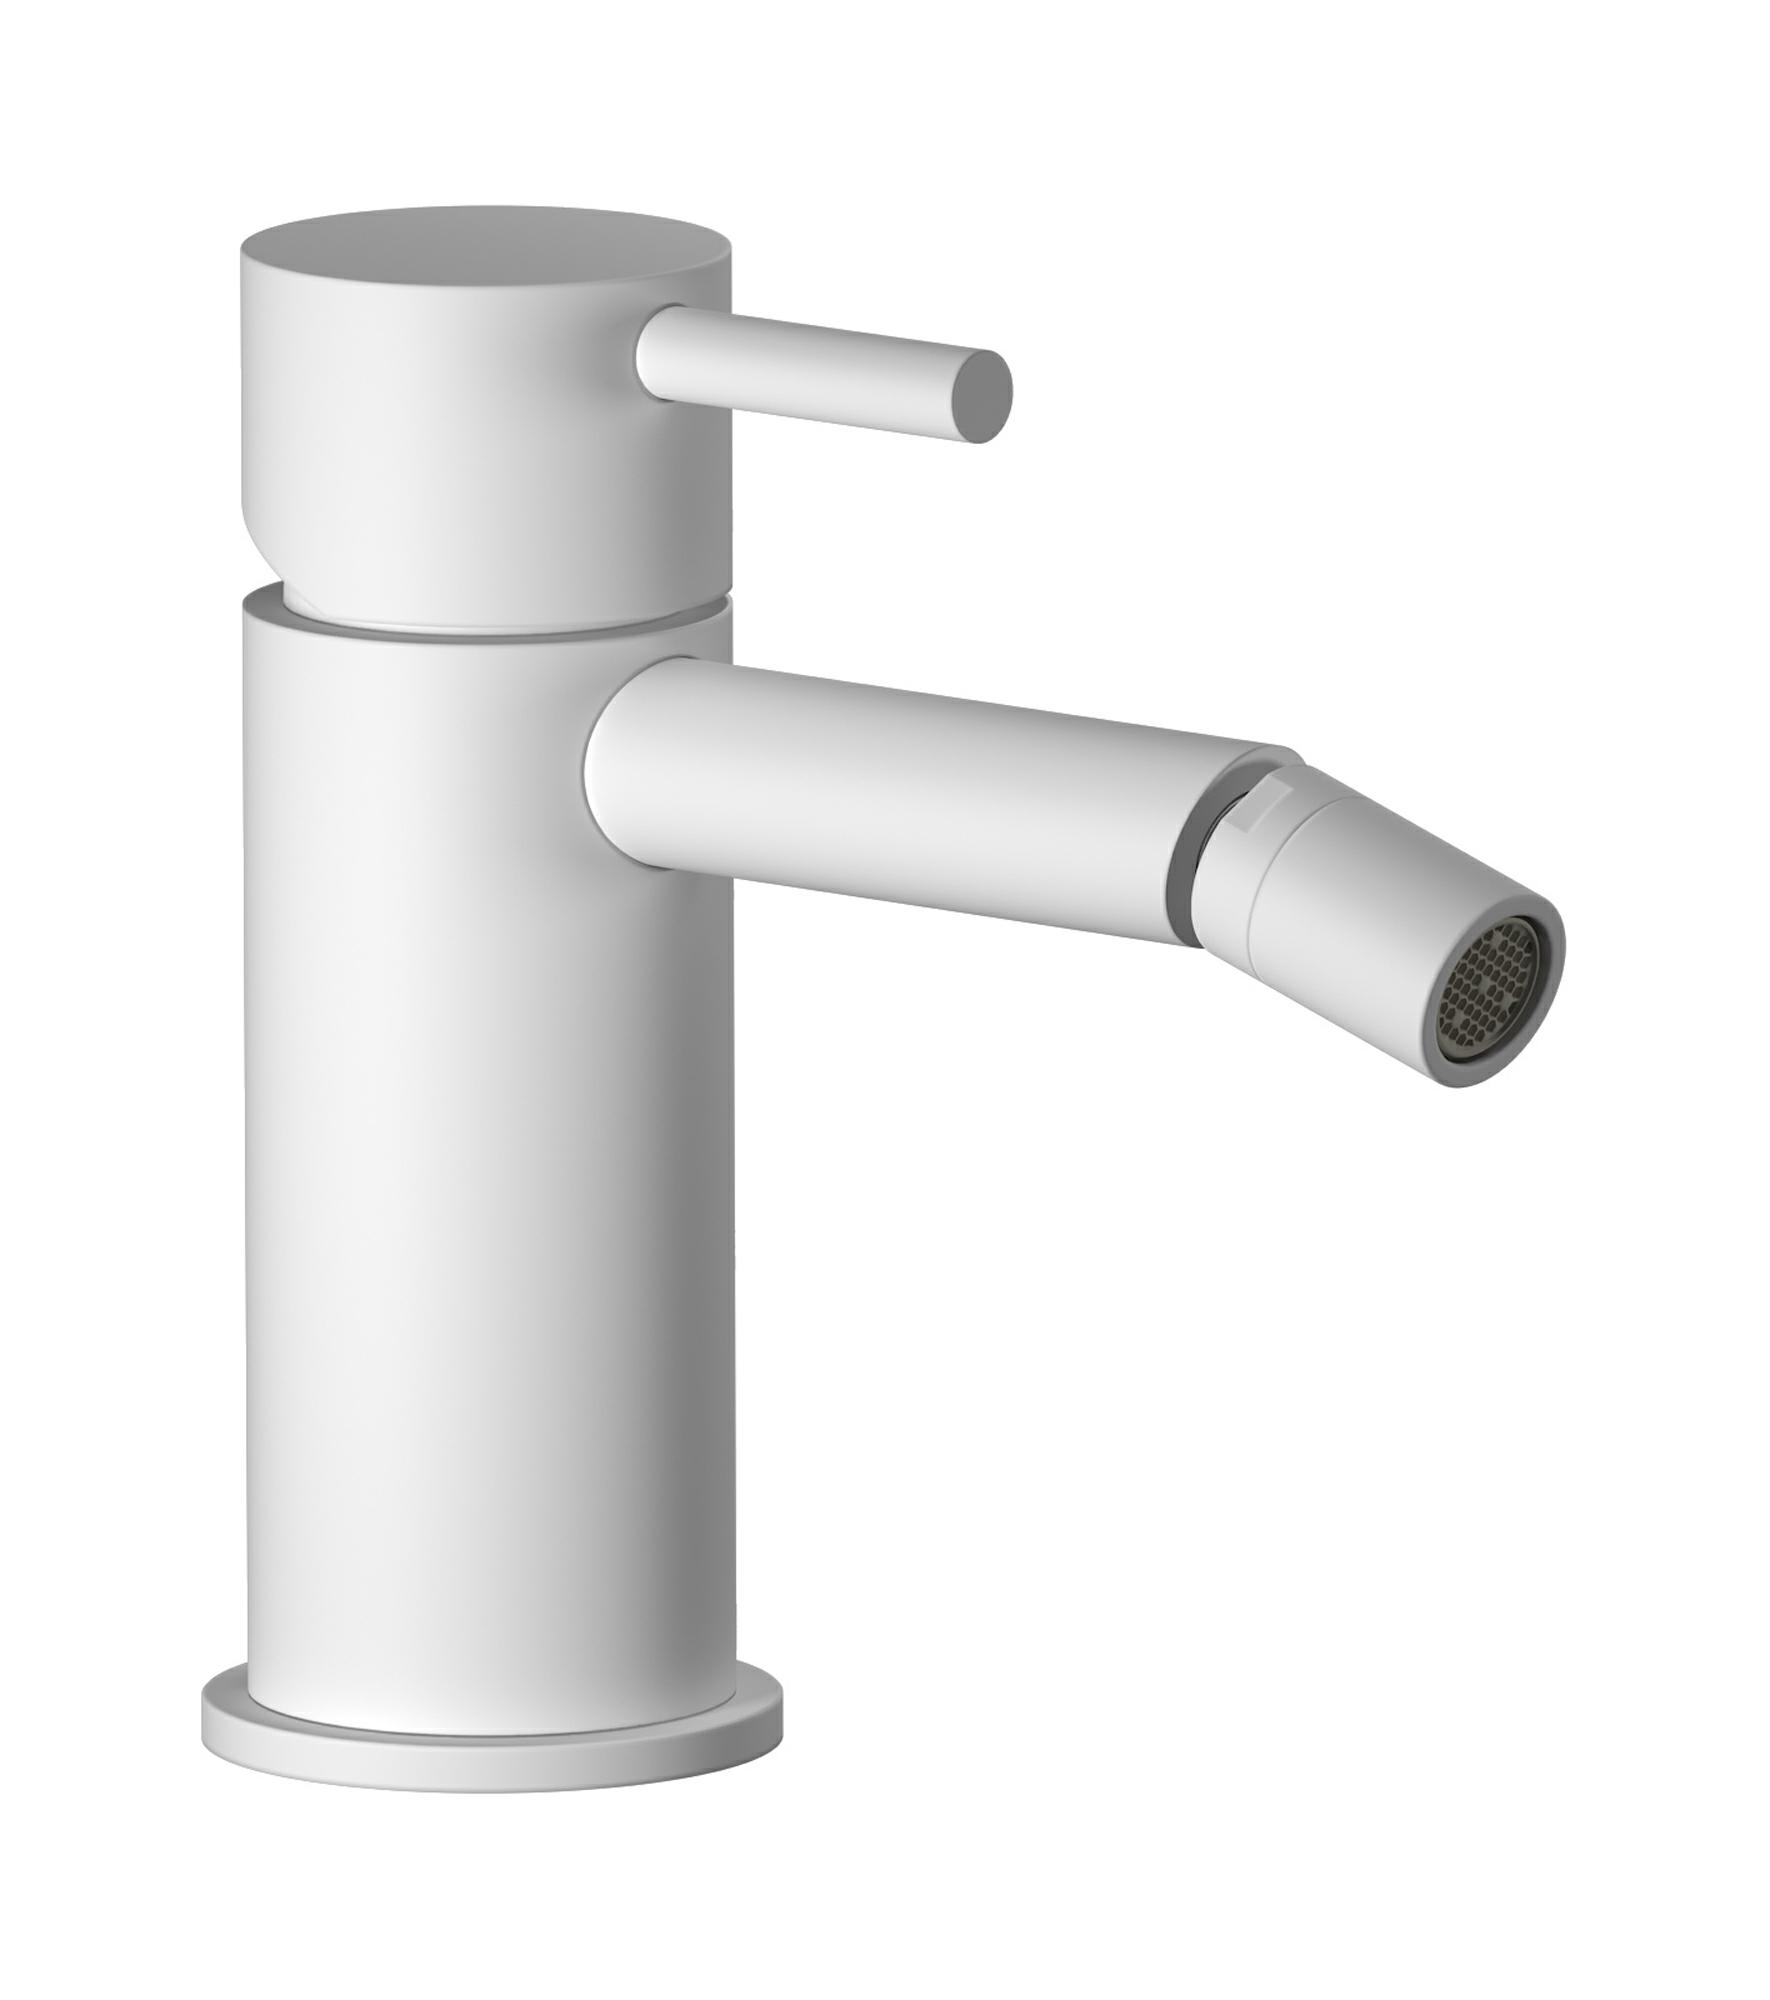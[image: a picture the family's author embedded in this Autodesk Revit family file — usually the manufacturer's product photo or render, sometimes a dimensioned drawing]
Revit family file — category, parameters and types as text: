
# Revit family: MT220
name_source: partatom
category: Apparecchi idraulici
units: mm (PartAtom-declared; Revit-internal decimal feet)

## family parameters
Basato su piano di lavoro = No
Condiviso = No
Mantieni orientamento annotazione = No
Numero OmniClass = 23.45.55.17
Punto di calcolo locali = No
Quota connettore circolare = Usa diametro
Sempre verticale = Sì
Taglio con vuoti quando caricato = No
Tipo di parte = Normale
Titolo OmniClass = Mixing Faucets

## types (13) — shared parameters
Cold water inlet = 10 mm  [stored 0.0328084 ft]
Commenti sul tipo = Bidet mixer
Connessione CW = No
Connessione HW = No
Connessione di scarico = No
Connessione di ventilazione = No
Descrizione = Monohole bidet mixer complete with drain
Hot water inlet = 10 mm  [stored 0.0328084 ft]
Produttore = IB Rubinetterie S.p.A.
URL = https://www.weareib.it
zero-valued in all types: Prospetto di default

## per-type parameters (varying)
| type | Finishes surface | Immagine tipo | Modello |
| Chrome | IB_Chrome | MT220CC.jpg | MT220CC |
| Brushed nickel | IB_Brushed nickel | MT220SS.jpg | MT220SS |
| Matt white | IB_matt white | MT220BO.jpg | MT220BO |
| Matt black | IB_matt black | MT220NP.jpg | MT220NP |
| Natural brass | IB_Brass | MT220ON.jpg | MT220ON |
| Black chrome | IB_Black chrome | MT220CF.jpg | MT220CF |
| Brushed black chrome | IB_Brushed black chrome | MT220CS.jpg | MT220CS |
| Pale gold | IB_Pale gold | MT220II.jpg | MT220II |
| Brushed pale gold | IB_brushed pale gold | MT220IS.jpg | MT220IS |
| Rose gold | IB_Rose gold | MT220RS.jpg | MT220RS |
| Brushed rose gold | IB_Brushed rose gold | MT220SR.jpg | MT220SR |
| Gold | IB_gold | MT220OO.jpg | MT220OO |
| Brushed gold | IB_brushed gold | MT220OS.jpg | MT220OS |

note: [stored X ft] marks values corroborated as IEEE doubles in the binary element streams (Revit-internal decimal feet)
